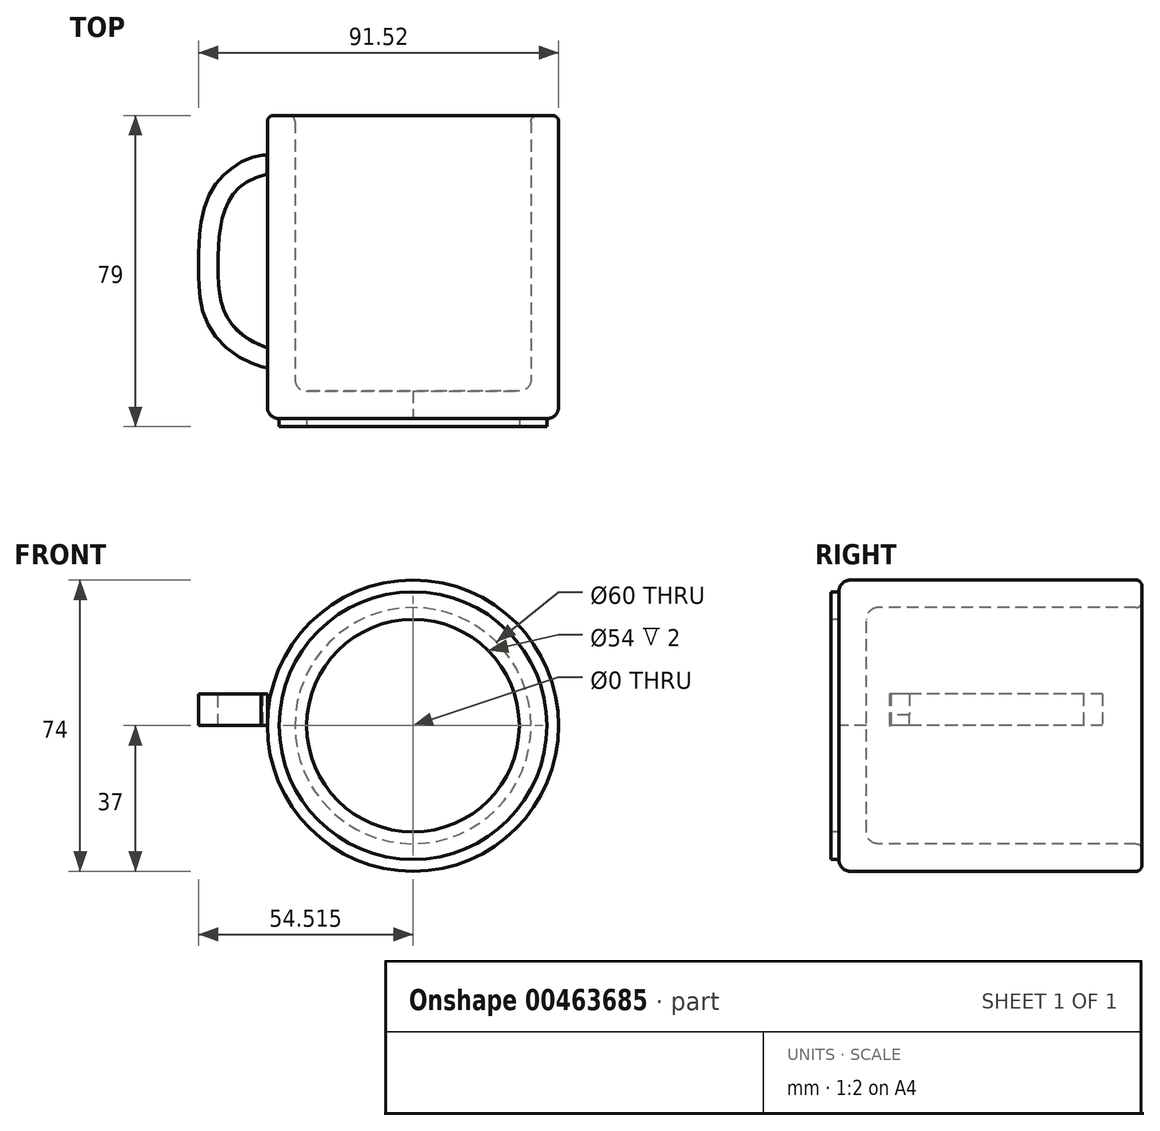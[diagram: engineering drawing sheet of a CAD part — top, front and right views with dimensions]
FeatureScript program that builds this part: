
annotation { "Feature Type Name" : "Feature", "Feature Type Description" : "" }
export const myFeature = defineFeature(function(context is Context, id is Id, definition is map)
    precondition{}
    {
        {
            var Q0;
            Q0=qCreatedBy(makeId("Top.planeOp"),FACE);
            var sketch = newSketch(context, id + "F0", { "sketchPlane" : qUnion([Q0])});
            skLineSegment(sketch, "E0", {"start": v(-47.14, 51.24) * mm, "end": v(-47.14, -21.26) * mm});
            skLineSegment(sketch, "E1", {"start": v(-37.14, -24.26) * mm, "end": v(-10.14, -24.26) * mm});
            skLineSegment(sketch, "E2", {"start": v(-10.14, -24.26) * mm, "end": v(-10.14, -17.26) * mm});
            skLineSegment(sketch, "E3", {"start": v(-10.14, -17.26) * mm, "end": v(-37.14, -17.26) * mm});
            skLineSegment(sketch, "E4", {"start": v(-40.14, -14.26) * mm, "end": v(-40.14, 51.24) * mm});
            skLineSegment(sketch, "E5", {"start": v(-41.64, 52.74) * mm, "end": v(-45.64, 52.74) * mm});
            skPoint(sketch, "E6.visualSharp", {"position": v(-47.14, 52.74) * mm});
            skArc(sketch, "E6.filletArc", {"start": v(-45.64, 52.74) * mm, "mid": v(-46.7, 52.3) * mm, "end": v(-47.14, 51.24) * mm});
            skPoint(sketch, "E7.visualSharp", {"position": v(-40.14, 52.74) * mm});
            skArc(sketch, "E7.filletArc", {"start": v(-40.14, 51.24) * mm, "mid": v(-40.58, 52.3) * mm, "end": v(-41.64, 52.74) * mm});
            skPoint(sketch, "E8.visualSharp", {"position": v(-47.14, -24.26) * mm});
            skPoint(sketch, "E9.visualSharp", {"position": v(-40.14, -17.26) * mm});
            skArc(sketch, "E9.filletArc", {"start": v(-40.14, -14.26) * mm, "mid": v(-39.26, -16.38) * mm, "end": v(-37.14, -17.26) * mm});
            skArc(sketch, "E10.filletArc", {"start": v(-47.14, -21.26) * mm, "mid": v(-46.26, -23.38) * mm, "end": v(-44.14, -24.26) * mm});
            skLineSegment(sketch, "E11", {"start": v(-44.14, -24.26) * mm, "end": v(-44.14, -26.26) * mm});
            skLineSegment(sketch, "E12", {"start": v(-44.14, -26.26) * mm, "end": v(-37.14, -26.26) * mm});
            skLineSegment(sketch, "E13", {"start": v(-37.14, -26.26) * mm, "end": v(-37.14, -24.26) * mm});
            skSolve(sketch);
        }
        {
            var Q0;
            Q0=qCreatedBy(makeId("Top.planeOp"),FACE);
            var sketch = newSketch(context, id + "F1", { "sketchPlane" : qUnion([Q0])});
            skLineSegment(sketch, "E14", {"start": v(-10.14, -24.25) * mm, "end": v(-10.14, 36.87) * mm});
            skSolve(sketch);
        }
        {
            var Q0;
            Q0=makeQuery(id+"F0.imprint","IMPRINT",FACE,{"disambiguationData":[TD([[makeQuery(id+"F0.imprint","IMPRINT",EDGE,{"derivedFrom":sQuery(id+"F0.wireOp",EDGE,"E0")}),1.0]])]});
            var Q1;
            Q1=sQuery(id+"F1.wireOp",EDGE,"E14");
            revolve(context, id + "F2", {"entities" : qUnion([Q0]), "axis" : qUnion([Q1]), "revolveType" : RevolveType.FULL});
        }
        {
            var Q0;
            Q0=qCreatedBy(makeId("Top.planeOp"),FACE);
            var sketch = newSketch(context, id + "F3", { "sketchPlane" : qUnion([Q0])});
            skFitSpline(sketch, "E15", {"points": [v(-47.26, 37.9) * mm, v(-59.62, 15.97) * mm, v(-47.04, -6.29) * mm], "startDerivative": vector(-69.72, -16.1) * mm, "endDerivative": vector(74.5, -26.6) * mm});
            skFitSpline(sketch, "E16.0", {"points": [v(-48.39, 42.77) * mm, v(-50.17, 42.36) * mm, v(-52.64, 41.5) * mm, v(-55.5, 39.87) * mm, v(-57.4, 38.43) * mm, v(-59.03, 36.8) * mm, v(-60.87, 34.43) * mm, v(-62.5, 31.23) * mm, v(-63.67, 27.29) * mm, v(-64.18, 24.03) * mm, v(-64.4, 21.47) * mm, v(-64.52, 19.58) * mm, v(-64.57, 18.04) * mm, v(-64.6, 16.84) * mm, v(-64.62, 15.95) * mm, v(-64.63, 15.06) * mm, v(-64.64, 13.87) * mm, v(-64.64, 12.36) * mm, v(-64.59, 10.52) * mm, v(-64.42, 8.03) * mm, v(-63.97, 4.87) * mm, v(-62.8, 1.01) * mm, v(-60.76, -2.74) * mm, v(-57.72, -6.11) * mm, v(-53.75, -8.9) * mm, v(-50.5, -10.36) * mm, v(-48.72, -11) * mm]});
            skLineSegment(sketch, "E17", {"start": v(-48.39, 42.77) * mm, "end": v(-47.15, 42.77) * mm});
            skLineSegment(sketch, "E18", {"start": v(-47.15, 42.77) * mm, "end": v(-47.26, 37.9) * mm});
            skLineSegment(sketch, "E19", {"start": v(-47.04, -6.29) * mm, "end": v(-47.04, -11.4) * mm});
            skLineSegment(sketch, "E20", {"start": v(-47.04, -11.4) * mm, "end": v(-48.72, -11) * mm});
            skSolve(sketch);
        }
        {
            var Q0;
            Q0 = qSketchRegion(id + "F3", true);
            extrude(context, id + "F4", {"entities" : qUnion([Q0]), "operationType" : NewBodyOperationType.ADD, "depth" : 8 * mm});
        }
    });
